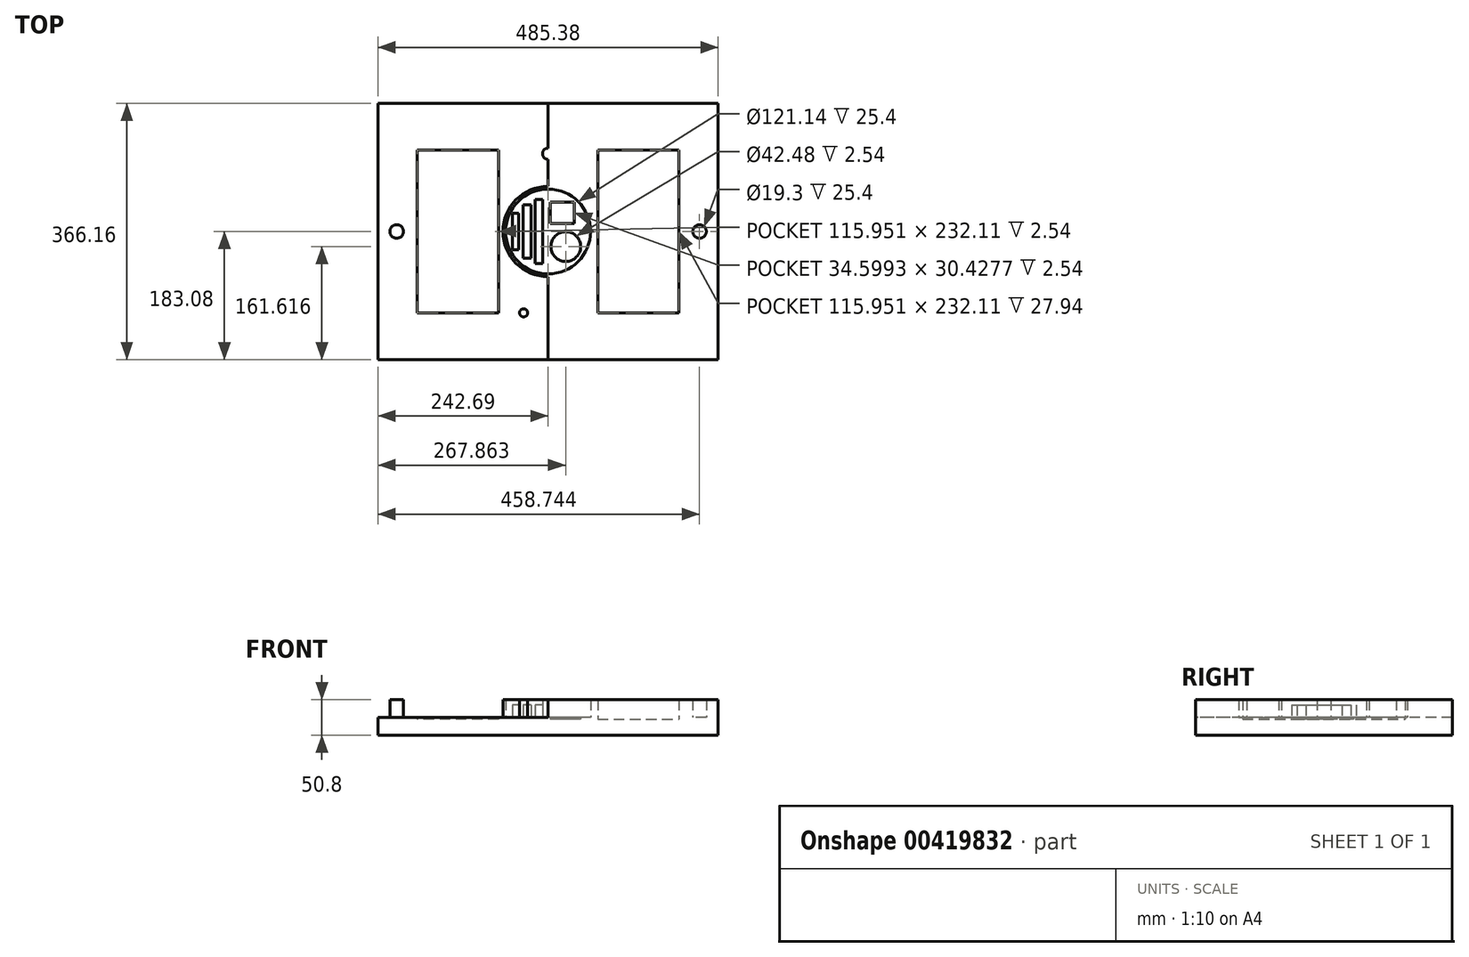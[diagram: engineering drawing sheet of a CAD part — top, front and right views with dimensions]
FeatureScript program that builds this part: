
annotation { "Feature Type Name" : "Feature", "Feature Type Description" : "" }
export const myFeature = defineFeature(function(context is Context, id is Id, definition is map)
    precondition{}
    {
        {
            var Q0;
            Q0=qCreatedBy(makeId("Top.planeOp"),FACE);
            var sketch = newSketch(context, id + "F0", { "sketchPlane" : qUnion([Q0])});
            skCircle(sketch, "E0", {"center": v(0, 0) * mm, "radius": 60.57 * mm});
            skLineSegment(sketch, "E1", {"start": v(0, 60.57) * mm, "end": v(0, -60.57) * mm});
            skLineSegment(sketch, "E2.bottom", {"start": v(70.73, -116.05) * mm, "end": v(186.69, -116.05) * mm});
            skLineSegment(sketch, "E2.top", {"start": v(70.73, 116.05) * mm, "end": v(186.69, 116.05) * mm});
            skLineSegment(sketch, "E2.left", {"start": v(70.73, -116.05) * mm, "end": v(70.73, 116.05) * mm});
            skLineSegment(sketch, "E2.right", {"start": v(186.69, -116.05) * mm, "end": v(186.69, 116.05) * mm});
            skPoint(sketch, "E2.middle", {"position": v(128.71, 0) * mm});
            skLineSegment(sketch, "E3.MirrorCS", {"start": v(-186.69, -116.05) * mm, "end": v(-186.69, 116.05) * mm});
            skLineSegment(sketch, "E4.MirrorCS", {"start": v(-70.73, 116.05) * mm, "end": v(-186.69, 116.05) * mm});
            skLineSegment(sketch, "E5.MirrorCS", {"start": v(-70.73, -116.05) * mm, "end": v(-70.73, 116.05) * mm});
            skLineSegment(sketch, "E6.MirrorCS", {"start": v(-70.73, -116.05) * mm, "end": v(-186.69, -116.05) * mm});
            skLineSegment(sketch, "E7.bottom", {"start": v(-7.63, -45.86) * mm, "end": v(-18.28, -45.86) * mm});
            skLineSegment(sketch, "E7.top", {"start": v(-7.63, 45.86) * mm, "end": v(-18.28, 45.86) * mm});
            skLineSegment(sketch, "E7.left", {"start": v(-7.63, -45.86) * mm, "end": v(-7.63, 45.86) * mm});
            skLineSegment(sketch, "E7.right", {"start": v(-18.28, -45.86) * mm, "end": v(-18.28, 45.86) * mm});
            skPoint(sketch, "E7.middle", {"position": v(-12.95, 0) * mm});
            skLineSegment(sketch, "E8.bottom", {"start": v(-24.58, -38.38) * mm, "end": v(-35.47, -38.38) * mm});
            skLineSegment(sketch, "E8.top", {"start": v(-24.58, 38.38) * mm, "end": v(-35.47, 38.38) * mm});
            skLineSegment(sketch, "E8.left", {"start": v(-24.58, -38.38) * mm, "end": v(-24.58, 38.38) * mm});
            skLineSegment(sketch, "E8.right", {"start": v(-35.47, -38.38) * mm, "end": v(-35.47, 38.38) * mm});
            skPoint(sketch, "E8.middle", {"position": v(-30.03, 0) * mm});
            skLineSegment(sketch, "E9.bottom", {"start": v(-42.02, -25.77) * mm, "end": v(-50.64, -25.77) * mm});
            skLineSegment(sketch, "E9.top", {"start": v(-42.02, 25.77) * mm, "end": v(-50.64, 25.77) * mm});
            skLineSegment(sketch, "E9.left", {"start": v(-42.02, -25.77) * mm, "end": v(-42.02, 25.77) * mm});
            skLineSegment(sketch, "E9.right", {"start": v(-50.64, -25.77) * mm, "end": v(-50.64, 25.77) * mm});
            skPoint(sketch, "E9.middle", {"position": v(-46.33, 0) * mm});
            skCircle(sketch, "E10", {"center": v(0, 0) * mm, "radius": 64.48 * mm});
            skCircle(sketch, "E11", {"center": v(25.17, -21.46) * mm, "radius": 21.24 * mm});
            skLineSegment(sketch, "E12.bottom", {"start": v(37.5, 42.17) * mm, "end": v(2.9, 42.17) * mm});
            skLineSegment(sketch, "E12.top", {"start": v(37.5, 11.74) * mm, "end": v(2.9, 11.74) * mm});
            skLineSegment(sketch, "E12.left", {"start": v(37.5, 42.17) * mm, "end": v(37.5, 11.74) * mm});
            skLineSegment(sketch, "E12.right", {"start": v(2.9, 42.17) * mm, "end": v(2.9, 11.74) * mm});
            skPoint(sketch, "E12.middle", {"position": v(20.2, 26.95) * mm});
            skLineSegment(sketch, "E13.bottom", {"start": v(242.7, 183.08) * mm, "end": v(-242.7, 183.08) * mm});
            skLineSegment(sketch, "E13.top", {"start": v(242.7, -183.08) * mm, "end": v(-242.7, -183.08) * mm});
            skLineSegment(sketch, "E13.left", {"start": v(242.7, 183.08) * mm, "end": v(242.7, -183.08) * mm});
            skLineSegment(sketch, "E13.right", {"start": v(-242.7, 183.08) * mm, "end": v(-242.7, -183.08) * mm});
            skFitSpline(sketch, "E14", {"points": [v(-8.35, -63.94) * mm, v(0, -112.17) * mm, v(0, -183.08) * mm], "startDerivative": vector(22.56, -101.05) * mm, "endDerivative": vector(-5.02, -136.27) * mm});
            skFitSpline(sketch, "E15", {"points": [v(0, -64.48) * mm, v(9.84, -112.17) * mm, v(10.1, -183.08) * mm], "startDerivative": vector(26.53, -99.7) * mm, "endDerivative": vector(-5.34, -136.35) * mm, "construction": true});
            skSolve(sketch);
        }
        {
            var Q0;
            Q0 = qSketchRegion(id + "F0", true);
            extrude(context, id + "F1", {"entities" : qUnion([Q0]), "depth" : 25.4 * mm});
        }
        {
            var Q0;
            Q0=makeQuery(id+"F0.imprint","IMPRINT",FACE,{"disambiguationData":[TD([[makeQuery(id+"F0.imprint","IMPRINT",EDGE,{"derivedFrom":sQuery(id+"F0.wireOp",EDGE,"E10")}),1.0]])]});
            extrude(context, id + "F2", {"entities" : qUnion([Q0]), "operationType" : NewBodyOperationType.ADD, "depth" : 50.8 * mm});
        }
        {
            var Q0;
            {var subQ0=sQuery(id+"F0.wireOp",EDGE,"E1");Q0=makeQuery(id+"F0.imprint","IMPRINT",FACE,{"disambiguationData":[TD([[makeQuery(id+"F0.imprint","IMPRINT",EDGE,{"derivedFrom":subQ0}),-1.0]])]});}
            var Q1;
            {var subQ0=sQuery(id+"F0.wireOp",EDGE,"E1");Q1=makeQuery(id+"F0.imprint","IMPRINT",FACE,{"disambiguationData":[TD([[makeQuery(id+"F0.imprint","IMPRINT",EDGE,{"derivedFrom":subQ0}),1.0]])]});}
            extrude(context, id + "F3", {"entities" : qUnion([Q0, Q1]), "operationType" : NewBodyOperationType.ADD, "depth" : 25.4 * mm});
        }
        {
            var Q0;
            Q0=makeQuery(id+"F0.imprint","IMPRINT",FACE,{"disambiguationData":[TD([[makeQuery(id+"F0.imprint","IMPRINT",EDGE,{"derivedFrom":sQuery(id+"F0.wireOp",EDGE,"E9.bottom")}),-1.0]])]});
            var Q1;
            Q1=makeQuery(id+"F0.imprint","IMPRINT",FACE,{"disambiguationData":[TD([[makeQuery(id+"F0.imprint","IMPRINT",EDGE,{"derivedFrom":sQuery(id+"F0.wireOp",EDGE,"E8.bottom")}),-1.0]])]});
            var Q2;
            Q2=makeQuery(id+"F0.imprint","IMPRINT",FACE,{"disambiguationData":[TD([[makeQuery(id+"F0.imprint","IMPRINT",EDGE,{"derivedFrom":sQuery(id+"F0.wireOp",EDGE,"E7.bottom")}),-1.0]])]});
            extrude(context, id + "F4", {"entities" : qUnion([Q0, Q1, Q2]), "operationType" : NewBodyOperationType.ADD, "depth" : 43.18 * mm});
        }
        {
            var Q0;
            Q0=makeQuery(id+"F0.imprint","IMPRINT",FACE,{"disambiguationData":[TD([[makeQuery(id+"F0.imprint","IMPRINT",EDGE,{"derivedFrom":sQuery(id+"F0.wireOp",EDGE,"E3.MirrorCS")}),-1.0]])]});
            var Q1;
            Q1=makeQuery(id+"F0.imprint","IMPRINT",FACE,{"disambiguationData":[TD([[makeQuery(id+"F0.imprint","IMPRINT",EDGE,{"derivedFrom":sQuery(id+"F0.wireOp",EDGE,"E12.bottom")}),1.0]])]});
            var Q2;
            Q2=makeQuery(id+"F0.imprint","IMPRINT",FACE,{"disambiguationData":[TD([[makeQuery(id+"F0.imprint","IMPRINT",EDGE,{"derivedFrom":sQuery(id+"F0.wireOp",EDGE,"E11")}),1.0]])]});
            var Q3;
            Q3=makeQuery(id+"F0.imprint","IMPRINT",FACE,{"disambiguationData":[TD([[makeQuery(id+"F0.imprint","IMPRINT",EDGE,{"derivedFrom":sQuery(id+"F0.wireOp",EDGE,"E2.bottom")}),1.0]])]});
            extrude(context, id + "F5", {"entities" : qUnion([Q0, Q1, Q2, Q3]), "operationType" : NewBodyOperationType.ADD, "depth" : 22.86 * mm});
        }
        {
            var Q0;
            Q0=makeQuery(id+"F1.opExtrude","CAP_FACE",FACE,{"disambiguationData":[OSD([sQuery(id+"F0.wireOp",EDGE,"E2.bottom"),sQuery(id+"F0.wireOp",EDGE,"E2.top"),sQuery(id+"F0.wireOp",EDGE,"E2.left"),sQuery(id+"F0.wireOp",EDGE,"E2.right"),sQuery(id+"F0.wireOp",EDGE,"E3.MirrorCS"),sQuery(id+"F0.wireOp",EDGE,"E4.MirrorCS"),sQuery(id+"F0.wireOp",EDGE,"E5.MirrorCS"),sQuery(id+"F0.wireOp",EDGE,"E6.MirrorCS"),sQuery(id+"F0.wireOp",EDGE,"E10"),sQuery(id+"F0.wireOp",EDGE,"E13.bottom"),sQuery(id+"F0.wireOp",EDGE,"E13.top"),sQuery(id+"F0.wireOp",EDGE,"E13.left"),sQuery(id+"F0.wireOp",EDGE,"E13.right")])],"isStart":false});
            var sketch = newSketch(context, id + "F6", { "sketchPlane" : qUnion([Q0])});
            skCircle(sketch, "E16", {"center": v(0, 111) * mm, "radius": 8.04 * mm});
            skCircle(sketch, "E17", {"center": v(-216.05, 0) * mm, "radius": 9.65 * mm});
            skCircle(sketch, "E18", {"center": v(-35, -116.05) * mm, "radius": 5.8 * mm});
            skLineSegment(sketch, "E19", {"start": v(0, 183.08) * mm, "end": v(0, -183.08) * mm});
            skCircle(sketch, "E20.MirrorC", {"center": v(216.05, 0) * mm, "radius": 9.65 * mm});
            skSolve(sketch);
        }
        {
            var Q0;
            Q0=makeQuery(id+"F6.imprint","IMPRINT",FACE,{"disambiguationData":[TD([[makeQuery(id+"F6.imprint","IMPRINT",EDGE,{"derivedFrom":sQuery(id+"F6.wireOp",EDGE,"E17")}),1.0]])]});
            var Q1;
            Q1=makeQuery(id+"F6.imprint","IMPRINT",FACE,{"disambiguationData":[TD([[makeQuery(id+"F6.imprint","IMPRINT",EDGE,{"derivedFrom":sQuery(id+"F6.wireOp",EDGE,"E18")}),1.0]])]});
            var Q2;
            {var subQ0=sQuery(id+"F6.wireOp",EDGE,"E19");var subQ1=sQuery(id+"F6.wireOp",EDGE,"E16");var subQ2=makeQuery(id+"F6.imprint","INTERSECT",VERTEX,{"disambiguationData":[OD(0.0)],"derivedFrom":[subQ1,subQ0]});Q2=makeQuery(id+"F6.imprint","IMPRINT",FACE,{"disambiguationData":[TD([[makeQuery(id+"F6.imprint","IMPRINT",EDGE,{"disambiguationData":[TD([[subQ2,-1.0]])],"derivedFrom":subQ1}),1.0]])]});}
            var Q3;
            {var subQ0=sQuery(id+"F6.wireOp",EDGE,"E19");var subQ1=sQuery(id+"F6.wireOp",EDGE,"E16");var subQ2=makeQuery(id+"F6.imprint","INTERSECT",VERTEX,{"disambiguationData":[OD(0.0)],"derivedFrom":[subQ1,subQ0]});Q3=makeQuery(id+"F6.imprint","IMPRINT",FACE,{"disambiguationData":[TD([[makeQuery(id+"F6.imprint","IMPRINT",EDGE,{"disambiguationData":[TD([[subQ2,1.0]])],"derivedFrom":subQ1}),1.0]])]});}
            var Q4;
            Q4=makeQuery(id+"F6.imprint","IMPRINT",FACE,{"disambiguationData":[TD([[makeQuery(id+"F6.imprint","IMPRINT",EDGE,{"derivedFrom":sQuery(id+"F6.wireOp",EDGE,"E20.MirrorC")}),-1.0]])]});
            extrude(context, id + "F7", {"entities" : qUnion([Q0, Q1, Q2, Q3, Q4]), "operationType" : NewBodyOperationType.ADD, "depth" : 25.4 * mm});
        }
    });
